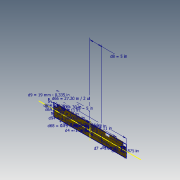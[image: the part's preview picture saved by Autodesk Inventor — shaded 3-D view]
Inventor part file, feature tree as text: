
AUTODESK INVENTOR PART (.ipt)
format: ipt  version: 2020.3 (Build 243373000, 373)  size: 203,264 bytes
history: native  units: in
note: dims shown in document units (in); Inventor stores cm internally (conversion verified against a paired STEP export)
features: sketch x3, hole x3, fillet x3, extrude x2, pattern_linear x1
ambient origin geometry x8: Origin, YZ Plane, XZ Plane, XY Plane, X Axis, Y Axis, Z Axis, Center Point
bodies: Solid1 (feature_tree)
feature tree (12):
  sketch  "Sketch1"  dims[d0=30.0in d1=5.0in]
  extrude  "Extrusion1"  Depth=5.0in
  hole  "Hole2"  [1 undecoded]
  fillet  "Fillet1"  Radius=1.26in
  hole  "Hole5"  [1 undecoded]
  fillet  "Fillet2"  Radius=5.0in
  extrude  "Extrusion2"  Depth=0.375in
  fillet  "Fillet3"  Radius=0.23in
  hole  "Hole6"  [1 undecoded]
  pattern_linear  "Rectangular Pattern2"  Spacing1=1.25in  [1 undecoded]
  sketch  "Sketch4"  dims[d2=1.73in d3=1.02in d4=1.26in]
  sketch  "Sketch5"  dims[d5=5.0in d7=1.26in d8=5.0in d9=0.413in d14=0.23in d15=0.0in d27=0.265in d28=0.75in d29=0.375in d30=0.25in d31=0.5635in d32=1.0in d33=0.8108in d34=0.375in d65=1.25in d66=13.6in d67=29.0in d68=0.75in d69=0.75in d70=0.276in d71=0.75in d72=0.433in d73=0.236in d74=90.0deg d75=1.0in d76=0.8108in d77=0.075in d78=1.9in d80=1.25in d81=0.0in d82=0.0in d83=7.261in d84=11.0in d85=11.0in d86=0.2in d87=1.125in d88=1.875in d89=0.0in d90=1.125in d91=13.5in d94=3.98in d105=0.075in d108=13.0in d109=13.0in d110=0.5in d111=0.123in d112=0.75in d113=0.375in d114=0.25in d115=0.5635in d116=1.0in d117=0.8108in d118=6.5in d119=6.5in d120=0.7874in d122=1.0in]
note: 4 required parameter values undecoded (feature->parameter linkage not recoverable at this tier; creation-order binding heuristic only, values carry confidence <= 0.55)
